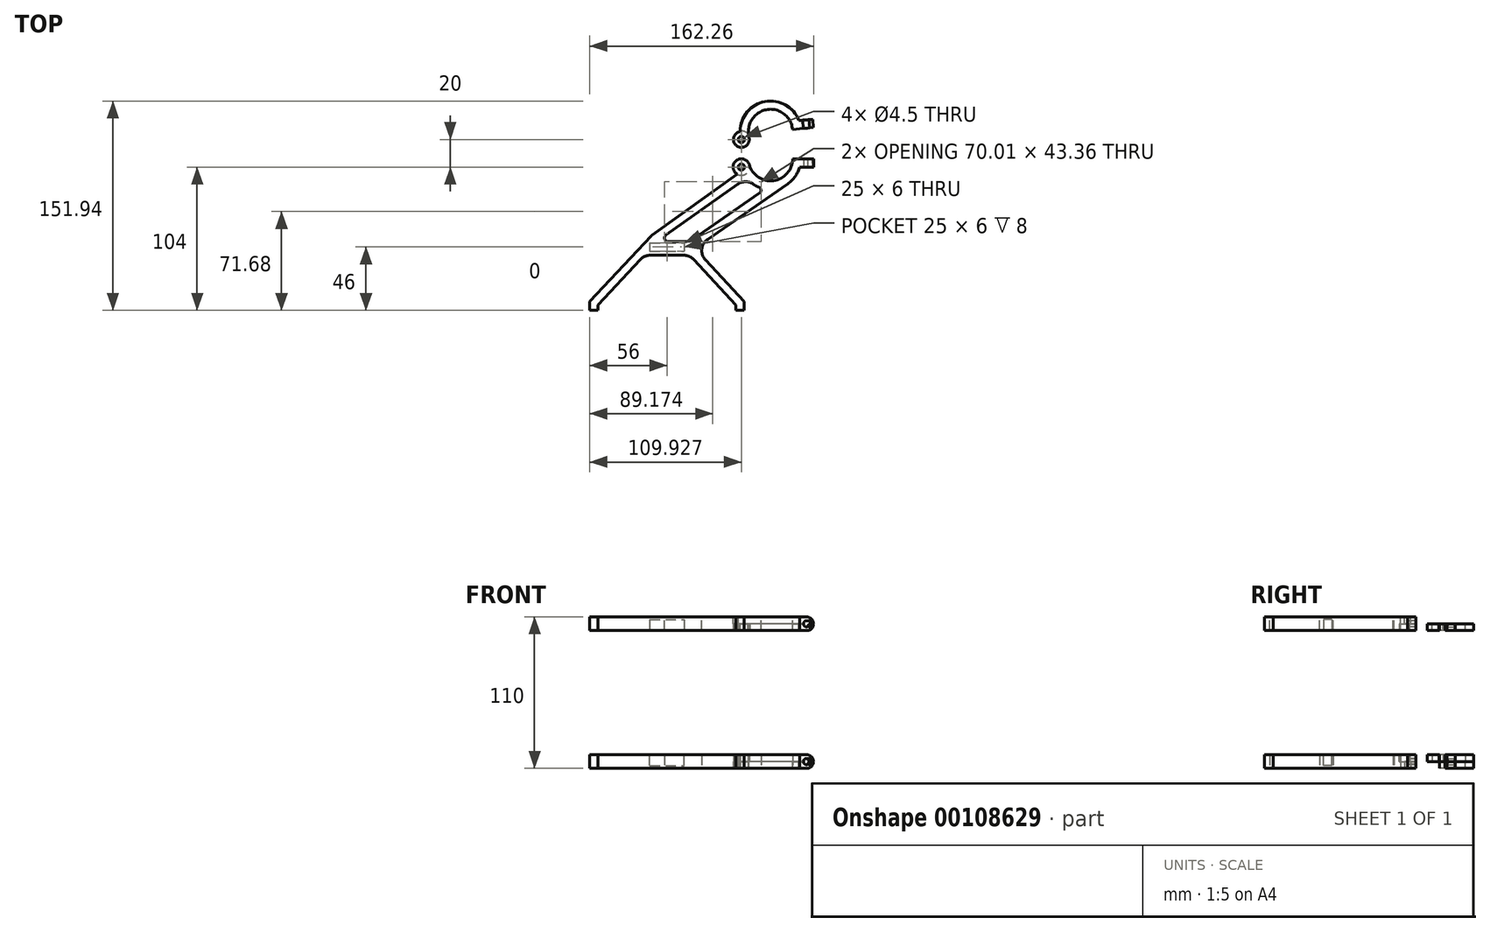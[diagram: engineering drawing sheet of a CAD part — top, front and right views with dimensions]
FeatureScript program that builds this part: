
annotation { "Feature Type Name" : "Feature", "Feature Type Description" : "" }
export const myFeature = defineFeature(function(context is Context, id is Id, definition is map)
    precondition{}
    {
        {
            var Q0;
            Q0=qCreatedBy(makeId("Top.planeOp"),FACE);
            var sketch = newSketch(context, id + "F0", { "sketchPlane" : qUnion([Q0])});
            skLineSegment(sketch, "E0", {"start": v(44.54, 54.16) * mm, "end": v(0, 6.36) * mm});
            skLineSegment(sketch, "E1", {"start": v(0, 6.36) * mm, "end": v(0, 0) * mm});
            skLineSegment(sketch, "E2", {"start": v(0, 0) * mm, "end": v(6, 0) * mm});
            skLineSegment(sketch, "E3", {"start": v(6, 0) * mm, "end": v(6, 4) * mm});
            skLineSegment(sketch, "E4", {"start": v(6, 4) * mm, "end": v(36.58, 36.82) * mm});
            skLineSegment(sketch, "E5", {"start": v(43.9, 40) * mm, "end": v(68.1, 40) * mm});
            skLineSegment(sketch, "E6", {"start": v(75.42, 36.82) * mm, "end": v(106, 4) * mm});
            skLineSegment(sketch, "E7", {"start": v(106, 4) * mm, "end": v(106, 0) * mm});
            skLineSegment(sketch, "E8", {"start": v(106, 0) * mm, "end": v(112, 0) * mm});
            skLineSegment(sketch, "E9", {"start": v(112, 0) * mm, "end": v(112, 6.36) * mm});
            skLineSegment(sketch, "E10", {"start": v(112, 6.36) * mm, "end": v(76, 45) * mm});
            skLineSegment(sketch, "E11", {"start": v(76, 45) * mm, "end": v(143.63, 91.92) * mm});
            skArc(sketch, "E12", {"start": v(109.93, 110) * mm, "mid": v(104.13, 105.55) * mm, "end": v(106.93, 98.8) * mm});
            skArc(sketch, "E13", {"start": v(115.7, 105.64) * mm, "mid": v(133.3, 94.15) * mm, "end": v(147.1, 110) * mm});
            skLineSegment(sketch, "E14", {"start": v(162.26, 110) * mm, "end": v(147.1, 110) * mm});
            skLineSegment(sketch, "E15", {"start": v(162.26, 104) * mm, "end": v(162.26, 110) * mm});
            skLineSegment(sketch, "E16", {"start": v(152.26, 104) * mm, "end": v(162.26, 104) * mm});
            skArc(sketch, "E17", {"start": v(143.63, 91.92) * mm, "mid": v(149, 97.21) * mm, "end": v(152.26, 104) * mm});
            skLineSegment(sketch, "E18", {"start": v(36, 45) * mm, "end": v(76, 45) * mm, "construction": true});
            skLineSegment(sketch, "E19", {"start": v(48.86, 50) * mm, "end": v(69.55, 50) * mm});
            skLineSegment(sketch, "E20", {"start": v(75.25, 51.78) * mm, "end": v(127.45, 88) * mm});
            skLineSegment(sketch, "E21", {"start": v(0, 0) * mm, "end": v(131.1, 110) * mm, "construction": true});
            skLineSegment(sketch, "E22", {"start": v(24.4, 32.54) * mm, "end": v(28.78, 28.45) * mm, "construction": true});
            skLineSegment(sketch, "E23", {"start": v(96.5, 23) * mm, "end": v(92.11, 18.9) * mm, "construction": true});
            skLineSegment(sketch, "E24", {"start": v(94.5, 65.14) * mm, "end": v(97.92, 60.21) * mm, "construction": true});
            skLineSegment(sketch, "E25", {"start": v(146.76, 106.78) * mm, "end": v(152.64, 105.57) * mm, "construction": true});
            skLineSegment(sketch, "E26", {"start": v(127.45, 88) * mm, "end": v(131.1, 88) * mm, "construction": true});
            skLineSegment(sketch, "E27", {"start": v(131.1, 88) * mm, "end": v(131.1, 94) * mm, "construction": true});
            skCircle(sketch, "E28", {"center": v(109.93, 104) * mm, "radius": 2.25 * mm});
            skLineSegment(sketch, "E29", {"start": v(109.93, 110) * mm, "end": v(109.93, 104) * mm, "construction": true});
            skLineSegment(sketch, "E30", {"start": v(106.93, 98.8) * mm, "end": v(109.93, 104) * mm, "construction": true});
            skPoint(sketch, "E31.visualSharp", {"position": v(36, 45) * mm});
            skPoint(sketch, "E32.visualSharp", {"position": v(39.54, 40) * mm});
            skArc(sketch, "E32.filletArc", {"start": v(43.9, 40) * mm, "mid": v(39.9, 39.17) * mm, "end": v(36.58, 36.82) * mm});
            skPoint(sketch, "E33.visualSharp", {"position": v(72.46, 40) * mm});
            skArc(sketch, "E33.filletArc", {"start": v(75.42, 36.82) * mm, "mid": v(72.1, 39.17) * mm, "end": v(68.1, 40) * mm});
            skPoint(sketch, "E34.visualSharp", {"position": v(72.68, 50) * mm});
            skArc(sketch, "E34.filletArc", {"start": v(69.55, 50) * mm, "mid": v(72.54, 50.46) * mm, "end": v(75.25, 51.78) * mm});
            skLineSegment(sketch, "E35", {"start": v(45.3, 54.83) * mm, "end": v(106.93, 98.8) * mm});
            skLineSegment(sketch, "E36", {"start": v(48.86, 50) * mm, "end": v(113.59, 96.19) * mm});
            skLineSegment(sketch, "E37", {"start": v(77.2, 77.6) * mm, "end": v(80.7, 72.71) * mm, "construction": true});
            skPoint(sketch, "E38", {"position": v(43.5, 49) * mm});
            skLineSegment(sketch, "E39", {"start": v(48.86, 50) * mm, "end": v(44.47, 54.1) * mm, "construction": true});
            skArc(sketch, "E40", {"start": v(113.59, 96.19) * mm, "mid": v(119.76, 90.8) * mm, "end": v(127.45, 88) * mm});
            skArc(sketch, "E41", {"start": v(115.7, 105.64) * mm, "mid": v(113.55, 108.79) * mm, "end": v(109.93, 110) * mm});
            skPoint(sketch, "E42.end.orphan", {"position": v(115.1, 110) * mm});
            skLineSegment(sketch, "E43", {"start": v(109.93, 110) * mm, "end": v(115.1, 110) * mm, "construction": true});
            skLineSegment(sketch, "E44", {"start": v(109.93, 104) * mm, "end": v(115.7, 105.64) * mm, "construction": true});
            skArc(sketch, "E45", {"start": v(118.48, 91.6) * mm, "mid": v(112.74, 93.36) * mm, "end": v(107.02, 91.5) * mm});
            skArc(sketch, "E46", {"start": v(85.49, 51.58) * mm, "mid": v(81.25, 44.44) * mm, "end": v(83.87, 36.55) * mm});
            skArc(sketch, "E47", {"start": v(55.22, 54.54) * mm, "mid": v(54.29, 51.74) * mm, "end": v(56.67, 50) * mm});
            skArc(sketch, "E48", {"start": v(123.12, 85) * mm, "mid": v(124.18, 87.32) * mm, "end": v(122.64, 89.36) * mm});
            skPoint(sketch, "E49.visualSharp", {"position": v(44.88, 54.53) * mm});
            skArc(sketch, "E49.filletArc", {"start": v(45.3, 54.83) * mm, "mid": v(44.9, 54.51) * mm, "end": v(44.54, 54.16) * mm});
            skSolve(sketch);
        }
        {
            var Q0;
            Q0=qSketchRegion(id+"F0",true);
            var Q1;
            {var subQ0=sQuery(id+"F0.wireOp",EDGE,"E47");Q1=makeQuery(id+"F0.imprint","IMPRINT",FACE,{"disambiguationData":[TD([[makeQuery(id+"F0.imprint","IMPRINT",EDGE,{"derivedFrom":subQ0}),-1.0]])]});}
            var Q2;
            {var subQ0=sQuery(id+"F0.wireOp",EDGE,"E45");Q2=makeQuery(id+"F0.imprint","IMPRINT",FACE,{"disambiguationData":[TD([[makeQuery(id+"F0.imprint","IMPRINT",EDGE,{"derivedFrom":subQ0}),-1.0]])]});}
            var Q3;
            {var subQ0=sQuery(id+"F0.wireOp",EDGE,"E48");Q3=makeQuery(id+"F0.imprint","IMPRINT",FACE,{"disambiguationData":[TD([[makeQuery(id+"F0.imprint","IMPRINT",EDGE,{"derivedFrom":subQ0}),-1.0]])]});}
            extrude(context, id + "F1", {"entities" : qUnion([Q0, Q1, Q2, Q3]), "endBound" : BoundingType.SYMMETRIC, "depth" : 10 * mm});
        }
        {
            var Q0;
            Q0=makeQuery(id+"F1.opExtrude","SWEPT_FACE",FACE,{"disambiguationData":[OSD([sQuery(id+"F0.wireOp",EDGE,"E16")])]});
            var sketch = newSketch(context, id + "F2", { "sketchPlane" : qUnion([Q0])});
            skCircle(sketch, "E50", {"center": v(157.26, 0) * mm, "radius": 2.25 * mm});
            skArc(sketch, "E51", {"start": v(157.26, -5) * mm, "mid": v(162.26, 0) * mm, "end": v(157.26, 5) * mm});
            skLineSegment(sketch, "E52", {"start": v(157.26, -5) * mm, "end": v(162.26, -5) * mm});
            skLineSegment(sketch, "E53", {"start": v(162.26, -5) * mm, "end": v(162.26, 5) * mm});
            skLineSegment(sketch, "E54", {"start": v(162.26, 5) * mm, "end": v(157.26, 5) * mm});
            skSolve(sketch);
        }
        {
            var Q0;
            Q0=qSketchRegion(id+"F2",true);
            extrude(context, id + "F3", {"entities" : qUnion([Q0]), "operationType" : NewBodyOperationType.REMOVE, "endBound" : BoundingType.THROUGH_ALL, "oppositeDirection" : true, "depth" : 25 * mm});
        }
        {
            var Q0;
            Q0=makeQuery(id+"F1.opExtrude","CAP_FACE",FACE,{"disambiguationData":[OSD([sQuery(id+"F0.wireOp",EDGE,"8654b762-f42e-4e54-a1a1-93a0492e9255"),sQuery(id+"F0.wireOp",EDGE,"E0"),sQuery(id+"F0.wireOp",EDGE,"E1"),sQuery(id+"F0.wireOp",EDGE,"E2"),sQuery(id+"F0.wireOp",EDGE,"E3"),sQuery(id+"F0.wireOp",EDGE,"E4"),sQuery(id+"F0.wireOp",EDGE,"E5"),sQuery(id+"F0.wireOp",EDGE,"E6"),sQuery(id+"F0.wireOp",EDGE,"E7"),sQuery(id+"F0.wireOp",EDGE,"E8"),sQuery(id+"F0.wireOp",EDGE,"E9"),sQuery(id+"F0.wireOp",EDGE,"E10"),sQuery(id+"F0.wireOp",EDGE,"E11"),sQuery(id+"F0.wireOp",EDGE,"E12"),sQuery(id+"F0.wireOp",EDGE,"E42"),sQuery(id+"F0.wireOp",EDGE,"E13"),sQuery(id+"F0.wireOp",EDGE,"E14"),sQuery(id+"F0.wireOp",EDGE,"E15"),sQuery(id+"F0.wireOp",EDGE,"E16"),sQuery(id+"F0.wireOp",EDGE,"E17"),sQuery(id+"F0.wireOp",EDGE,"E19"),sQuery(id+"F0.wireOp",EDGE,"E20"),sQuery(id+"F0.wireOp",EDGE,"3bac20cf-d173-4433-96f8-a9dfc64a6fbb"),sQuery(id+"F0.wireOp",EDGE,"0645d3f2-d8a1-47e1-a1c3-d69c6d73d3cb"),sQuery(id+"F0.wireOp",EDGE,"E28")])],"isStart":false});
            var sketch = newSketch(context, id + "F4", { "sketchPlane" : qUnion([Q0])});
            skLineSegment(sketch, "E55.bottom", {"start": v(43.5, 49) * mm, "end": v(68.5, 49) * mm});
            skLineSegment(sketch, "E55.top", {"start": v(43.5, 43) * mm, "end": v(68.5, 43) * mm});
            skLineSegment(sketch, "E55.left", {"start": v(43.5, 49) * mm, "end": v(43.5, 43) * mm});
            skLineSegment(sketch, "E55.right", {"start": v(68.5, 49) * mm, "end": v(68.5, 43) * mm});
            skPoint(sketch, "E56.0", {"position": v(43.5, 49) * mm});
            skSolve(sketch);
        }
        {
            var Q0;
            Q0=qSketchRegion(id+"F4",true);
            extrude(context, id + "F5", {"entities" : qUnion([Q0]), "operationType" : NewBodyOperationType.REMOVE, "oppositeDirection" : true, "depth" : 8 * mm});
        }
        {
            var Q0;
            Q0=makeQuery(id+"F1.opExtrude","CAP_FACE",FACE,{"disambiguationData":[OSD([sQuery(id+"F0.wireOp",EDGE,"E0"),sQuery(id+"F0.wireOp",EDGE,"E1"),sQuery(id+"F0.wireOp",EDGE,"E2"),sQuery(id+"F0.wireOp",EDGE,"E3"),sQuery(id+"F0.wireOp",EDGE,"E4"),sQuery(id+"F0.wireOp",EDGE,"E5"),sQuery(id+"F0.wireOp",EDGE,"E6"),sQuery(id+"F0.wireOp",EDGE,"E7"),sQuery(id+"F0.wireOp",EDGE,"E8"),sQuery(id+"F0.wireOp",EDGE,"E9"),sQuery(id+"F0.wireOp",EDGE,"E10"),sQuery(id+"F0.wireOp",EDGE,"E11"),sQuery(id+"F0.wireOp",EDGE,"E12"),sQuery(id+"F0.wireOp",EDGE,"E13"),sQuery(id+"F0.wireOp",EDGE,"E14"),sQuery(id+"F0.wireOp",EDGE,"E15"),sQuery(id+"F0.wireOp",EDGE,"E16"),sQuery(id+"F0.wireOp",EDGE,"E17"),sQuery(id+"F0.wireOp",EDGE,"E19"),sQuery(id+"F0.wireOp",EDGE,"E20"),sQuery(id+"F0.wireOp",EDGE,"E28"),sQuery(id+"F0.wireOp",EDGE,"E32.filletArc"),sQuery(id+"F0.wireOp",EDGE,"E33.filletArc"),sQuery(id+"F0.wireOp",EDGE,"E34.filletArc"),sQuery(id+"F0.wireOp",EDGE,"E35"),sQuery(id+"F0.wireOp",EDGE,"E36"),sQuery(id+"F0.wireOp",EDGE,"E40"),sQuery(id+"F0.wireOp",EDGE,"E41")])],"isStart":false});
            var sketch = newSketch(context, id + "F6", { "sketchPlane" : qUnion([Q0])});
            skCircle(sketch, "E57", {"center": v(109.93, 104) * mm, "radius": 6 * mm});
            skSolve(sketch);
        }
        {
            var Q0;
            Q0=qSketchRegion(id+"F6",true);
            extrude(context, id + "F7", {"entities" : qUnion([Q0]), "operationType" : NewBodyOperationType.REMOVE, "oppositeDirection" : true, "depth" : 5 * mm});
        }
        {
            var Q0;
            Q0=qCreatedBy(makeId("Top.planeOp"),FACE);
            var sketch = newSketch(context, id + "F8", { "sketchPlane" : qUnion([Q0])});
            skArc(sketch, "E58", {"start": v(147.05, 131.34) * mm, "mid": v(128.97, 145.8) * mm, "end": v(115.37, 127.08) * mm});
            skLineSegment(sketch, "E59", {"start": v(147.05, 131.34) * mm, "end": v(162.16, 132.66) * mm});
            skLineSegment(sketch, "E60", {"start": v(162.16, 132.66) * mm, "end": v(161.63, 138.64) * mm});
            skLineSegment(sketch, "E61", {"start": v(161.63, 138.64) * mm, "end": v(151.67, 137.77) * mm});
            skArc(sketch, "E62", {"start": v(151.67, 137.77) * mm, "mid": v(127, 151.56) * mm, "end": v(109.11, 129.7) * mm});
            skCircle(sketch, "E63", {"center": v(109.93, 124) * mm, "radius": 2.25 * mm});
            skCircle(sketch, "E64", {"center": v(109.93, 124) * mm, "radius": 6 * mm, "construction": true});
            skLineSegment(sketch, "E65", {"start": v(131.1, 129.94) * mm, "end": v(147.05, 131.34) * mm, "construction": true});
            skCircle(sketch, "E66.0", {"center": v(109.93, 124) * mm, "radius": 5.75 * mm});
            skLineSegment(sketch, "E67", {"start": v(109.93, 124) * mm, "end": v(115.7, 125.64) * mm, "construction": true});
            skLineSegment(sketch, "E68", {"start": v(131.1, 129.94) * mm, "end": v(115.1, 129.94) * mm, "construction": true});
            skCircle(sketch, "E69.0", {"center": v(109.93, 124) * mm, "radius": 6.25 * mm, "construction": true});
            skLineSegment(sketch, "E70", {"start": v(115.37, 127.08) * mm, "end": v(114.93, 126.83) * mm});
            skPoint(sketch, "E71", {"position": v(109.1, 129.94) * mm});
            skSolve(sketch);
        }
        {
            var Q0;
            Q0=qSketchRegion(id+"F8",true);
            extrude(context, id + "F9", {"entities" : qUnion([Q0]), "operationType" : NewBodyOperationType.ADD, "depth" : 5 * mm});
        }
        {
            var Q0;
            Q0=makeQuery(id+"F9.opExtrude","SWEPT_BODY",BODY,{"disambiguationData":[OSD([sQuery(id+"F8.wireOp",EDGE,"E58"),sQuery(id+"F8.wireOp",EDGE,"E59"),sQuery(id+"F8.wireOp",EDGE,"E60"),sQuery(id+"F8.wireOp",EDGE,"E61"),sQuery(id+"F8.wireOp",EDGE,"E62"),sQuery(id+"F8.wireOp",EDGE,"E63"),sQuery(id+"F8.wireOp",EDGE,"E64"),sQuery(id+"F8.wireOp",EDGE,"140aa226-682f-464c-9869-2b3d8af1f9aa")])]});
            var Q1;
            Q1=qCreatedBy(makeId("Top.planeOp"),FACE);
            mirror(context, id + "F10", {"operationType" : NewBodyOperationType.ADD, "entities" : qUnion([Q0]), "mirrorPlane" : qUnion([Q1])});
        }
        {
            var Q0;
            Q0=makeQuery(id+"F10.opPattern","COPY",FACE,{"derivedFrom":makeQuery(id+"F9.opExtrude","CAP_FACE",FACE,{"disambiguationData":[OSD([sQuery(id+"F8.wireOp",EDGE,"E58"),sQuery(id+"F8.wireOp",EDGE,"E59"),sQuery(id+"F8.wireOp",EDGE,"E60"),sQuery(id+"F8.wireOp",EDGE,"E61"),sQuery(id+"F8.wireOp",EDGE,"E62"),sQuery(id+"F8.wireOp",EDGE,"E63"),sQuery(id+"F8.wireOp",EDGE,"E64"),sQuery(id+"F8.wireOp",EDGE,"d96c58fc-394f-4b6e-b8ca-a2715a05a401")])],"isStart":false}),"instanceName":"1"});
            var sketch = newSketch(context, id + "F11", { "sketchPlane" : qUnion([Q0])});
            skCircle(sketch, "E72", {"center": v(109.93, -124) * mm, "radius": 6.25 * mm});
            skSolve(sketch);
        }
        {
            var Q0;
            Q0=qSketchRegion(id+"F11",true);
            extrude(context, id + "F12", {"entities" : qUnion([Q0]), "operationType" : NewBodyOperationType.REMOVE, "oppositeDirection" : true, "depth" : 5 * mm});
        }
        {
            var Q0;
            {var subQ0=makeQuery(id+"F9.opExtrude","SWEPT_FACE",FACE,{"disambiguationData":[OSD([sQuery(id+"F8.wireOp",EDGE,"E61")])]});Q0=makeQuery(id+"F10.boolean.opBoolean","MERGE",FACE,{"derivedFrom":[subQ0,makeQuery(id+"F10.opPattern","COPY",FACE,{"derivedFrom":subQ0,"instanceName":"1"})]});}
            var sketch = newSketch(context, id + "F13", { "sketchPlane" : qUnion([Q0])});
            skCircle(sketch, "E73", {"center": v(-168.1, 0) * mm, "radius": 2.25 * mm});
            skArc(sketch, "E74", {"start": v(-168.1, 5) * mm, "mid": v(-173.1, 0) * mm, "end": v(-168.1, -5) * mm});
            skLineSegment(sketch, "E75", {"start": v(-168.1, -5) * mm, "end": v(-173.1, -5) * mm});
            skLineSegment(sketch, "E76", {"start": v(-173.1, -5) * mm, "end": v(-173.1, 5) * mm});
            skLineSegment(sketch, "E77", {"start": v(-173.1, 5) * mm, "end": v(-168.1, 5) * mm});
            skSolve(sketch);
        }
        {
            var Q0;
            Q0=qSketchRegion(id+"F13",true);
            extrude(context, id + "F14", {"entities" : qUnion([Q0]), "operationType" : NewBodyOperationType.REMOVE, "endBound" : BoundingType.THROUGH_ALL, "oppositeDirection" : true, "depth" : 25 * mm});
        }
        {
            var Q0;
            Q0=qCreatedBy(makeId("Top.planeOp"),FACE);
            cPlane(context, id + "F15", {"entities" : qUnion([Q0]), "cplaneType" : CPlaneType.OFFSET, "offset" : 50 * mm, "width" : 150 * mm, "height" : 150 * mm});
        }
        {
            var Q0;
            Q0=makeQuery(id+"F1.opExtrude","SWEPT_BODY",BODY,{"disambiguationData":[OSD([sQuery(id+"F0.wireOp",EDGE,"8654b762-f42e-4e54-a1a1-93a0492e9255"),sQuery(id+"F0.wireOp",EDGE,"E0"),sQuery(id+"F0.wireOp",EDGE,"E1"),sQuery(id+"F0.wireOp",EDGE,"E2"),sQuery(id+"F0.wireOp",EDGE,"E3"),sQuery(id+"F0.wireOp",EDGE,"E4"),sQuery(id+"F0.wireOp",EDGE,"E5"),sQuery(id+"F0.wireOp",EDGE,"E6"),sQuery(id+"F0.wireOp",EDGE,"E7"),sQuery(id+"F0.wireOp",EDGE,"E8"),sQuery(id+"F0.wireOp",EDGE,"E9"),sQuery(id+"F0.wireOp",EDGE,"E10"),sQuery(id+"F0.wireOp",EDGE,"E11"),sQuery(id+"F0.wireOp",EDGE,"E12"),sQuery(id+"F0.wireOp",EDGE,"E42"),sQuery(id+"F0.wireOp",EDGE,"E13"),sQuery(id+"F0.wireOp",EDGE,"E14"),sQuery(id+"F0.wireOp",EDGE,"E15"),sQuery(id+"F0.wireOp",EDGE,"E16"),sQuery(id+"F0.wireOp",EDGE,"E17"),sQuery(id+"F0.wireOp",EDGE,"E19"),sQuery(id+"F0.wireOp",EDGE,"E20"),sQuery(id+"F0.wireOp",EDGE,"3bac20cf-d173-4433-96f8-a9dfc64a6fbb"),sQuery(id+"F0.wireOp",EDGE,"0645d3f2-d8a1-47e1-a1c3-d69c6d73d3cb"),sQuery(id+"F0.wireOp",EDGE,"E28")])]});
            var Q1;
            Q1=qCreatedBy(id+"F15.planeOp",FACE);
            mirror(context, id + "F16", {"entities" : qUnion([Q0]), "mirrorPlane" : qUnion([Q1])});
        }
        {
            var Q0;
            Q0=makeQuery(id+"F9.opExtrude","SWEPT_BODY",BODY,{"disambiguationData":[OSD([sQuery(id+"F8.wireOp",EDGE,"E58"),sQuery(id+"F8.wireOp",EDGE,"E59"),sQuery(id+"F8.wireOp",EDGE,"E60"),sQuery(id+"F8.wireOp",EDGE,"E61"),sQuery(id+"F8.wireOp",EDGE,"E62"),sQuery(id+"F8.wireOp",EDGE,"E63"),sQuery(id+"F8.wireOp",EDGE,"E64"),sQuery(id+"F8.wireOp",EDGE,"140aa226-682f-464c-9869-2b3d8af1f9aa")])]});
            var Q1;
            Q1=qCreatedBy(id+"F15.planeOp",FACE);
            mirror(context, id + "F17", {"entities" : qUnion([Q0]), "mirrorPlane" : qUnion([Q1])});
        }
    });
